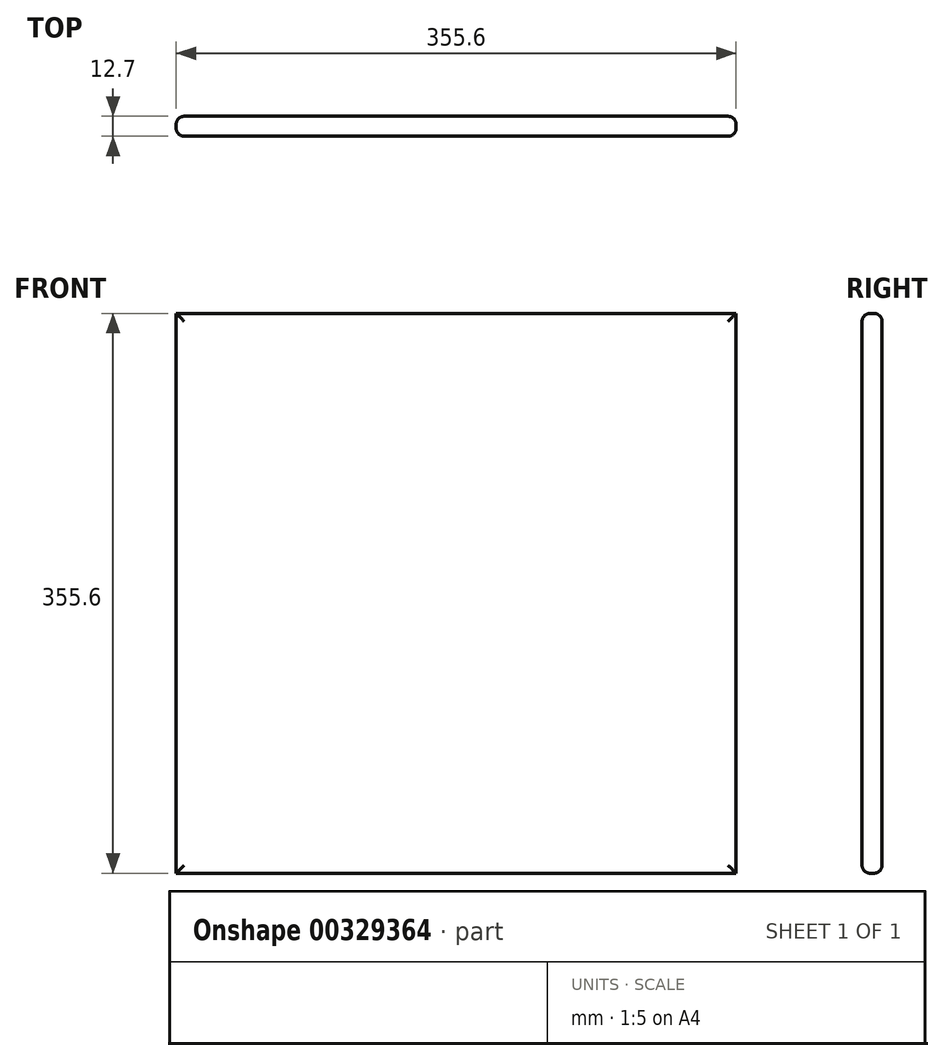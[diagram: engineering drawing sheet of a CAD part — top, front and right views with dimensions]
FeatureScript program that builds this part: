
annotation { "Feature Type Name" : "Feature", "Feature Type Description" : "" }
export const myFeature = defineFeature(function(context is Context, id is Id, definition is map)
    precondition{}
    {
        {
            var Q0;
            Q0=qCreatedBy(makeId("Front.planeOp"),FACE);
            var sketch = newSketch(context, id + "F0", { "sketchPlane" : qUnion([Q0])});
            skLineSegment(sketch, "E0.bottom", {"start": v(177.8, 177.8) * mm, "end": v(-177.8, 177.8) * mm});
            skLineSegment(sketch, "E0.top", {"start": v(177.8, -177.8) * mm, "end": v(-177.8, -177.8) * mm});
            skLineSegment(sketch, "E0.left", {"start": v(177.8, 177.8) * mm, "end": v(177.8, -177.8) * mm});
            skLineSegment(sketch, "E0.right", {"start": v(-177.8, 177.8) * mm, "end": v(-177.8, -177.8) * mm});
            skPoint(sketch, "E0.middle", {"position": v(0, 0) * mm});
            skSolve(sketch);
        }
        {
            var Q0;
            Q0 = qSketchRegion(id + "F0", true);
            var Q1;
            Q1=makeQuery(id+"F0.imprint","IMPRINT",FACE,{"disambiguationData":[TD([[makeQuery(id+"F0.imprint","IMPRINT",EDGE,{"derivedFrom":sQuery(id+"F0.wireOp",EDGE,"E0.bottom")}),1.0]])]});
            extrude(context, id + "F1", {"entities" : qUnion([Q0, Q1]), "depth" : 12.7 * mm});
        }
        {
            var Q0;
            Q0=makeQuery(id+"F1.opExtrude","CAP_FACE",FACE,{"disambiguationData":[OSD([sQuery(id+"F0.wireOp",EDGE,"E0.bottom"),sQuery(id+"F0.wireOp",EDGE,"E0.top"),sQuery(id+"F0.wireOp",EDGE,"E0.left"),sQuery(id+"F0.wireOp",EDGE,"E0.right")])],"isStart":false});
            var Q1;
            Q1=makeQuery(id+"F1.opExtrude","CAP_FACE",FACE,{"disambiguationData":[OSD([sQuery(id+"F0.wireOp",EDGE,"E0.bottom"),sQuery(id+"F0.wireOp",EDGE,"E0.top"),sQuery(id+"F0.wireOp",EDGE,"E0.left"),sQuery(id+"F0.wireOp",EDGE,"E0.right")])],"isStart":true});
            fillet(context, id + "F2", {"entities" : qUnion([Q0, Q1]), "radius" : 5.08 * mm, "tangentPropagation" : true, "allowEdgeOverflow" : false});
        }
    });
